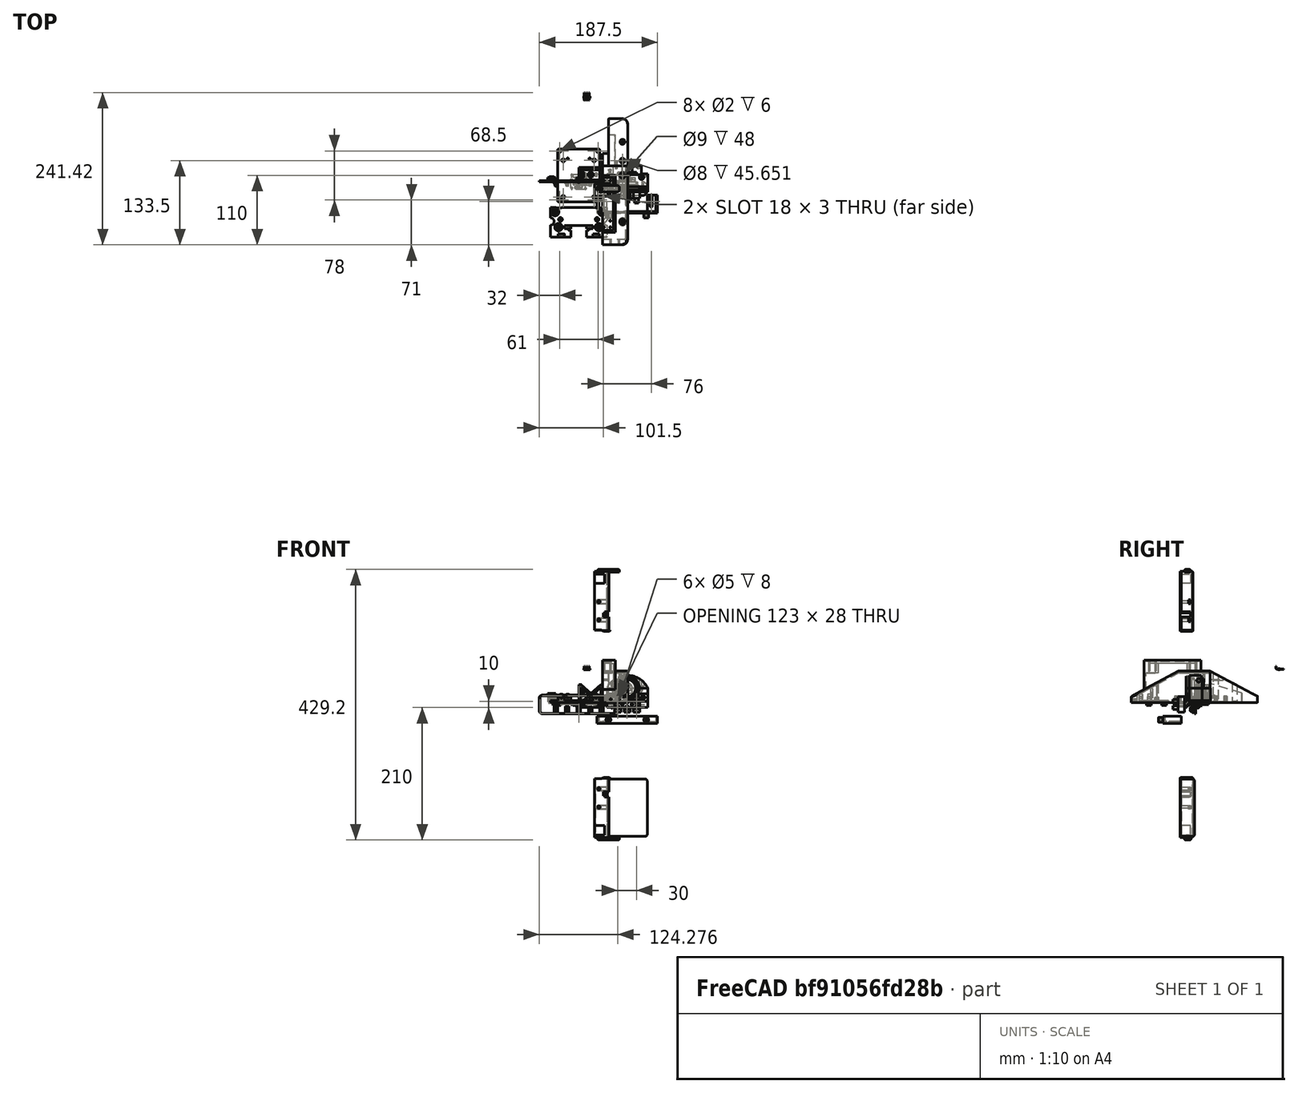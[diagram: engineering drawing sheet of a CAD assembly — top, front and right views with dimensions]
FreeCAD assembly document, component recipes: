
FREECAD ASSEMBLY — COMPONENT RECIPES ("BigOleYellow")

This assembly document has 16 components, labeled P0..P15 below (a component is one placed body or linked part). 9 of them carry a construction recipe — the FreeCAD feature program that regenerates the part from scratch, quoted from this document or its linked companion documents; the rest are supplied as boundary geometry only. No exploded tour is included for this assembly.
COMPONENT P0 — recipe-attached ("RearHullLeftBody", modeled in this document).
Construction recipe (the document's own serialized feature program — sketch geometry with constraints, then the solid features built on it; lengths are millimeters unless a unit is written):

FEATURE [Sketcher::SketchObject] Sketch015  label="RHLBBasePadSketch"
  FullyConstrained = true
  MapMode = 5
  Placement = pos=(0,0,0) rot=(0.57735,0.57735,0.57735;2.0944rad)
  Support = -> [YZ_Plane049]
  expr: Constraints[3] = Spreadsheet.rearhull_height
  expr: Constraints[4] = Spreadsheet.rearhull_length
  sketch-geometry (3):
    g0: LineSegment StartX=-2.83791e-11 StartY=40 StartZ=0 EndX=-2.83768e-11 EndY=0 EndZ=0
    g1: LineSegment StartX=-2.83768e-11 StartY=0 StartZ=0 EndX=75 EndY=-2e-16 EndZ=0
    g2: LineSegment StartX=75 StartY=-2e-16 StartZ=0 EndX=-2.83791e-11 EndY=40 EndZ=0
  constraints (7):
    c: Coincident(g0,g1)
    c: Coincident(g1,g2)
    c: Coincident(g2,g0)
    c: DistanceY(g0,g0) = 40
    c: DistanceX(g1,g1) = 75
    c: Tangent(g1,g-1)
    c: Tangent(g0,g-2)
FEATURE [PartDesign::Pad] Pad005  label="RHLBBasePad"
  Direction = (1,-2e-16,3e-16)
  Length = 30
  Length2 = 10
  Placement = pos=(0,0,0) rot=(1,1,1;2.0944rad)
  Profile = -> Sketch015
  ReferenceAxis = -> Sketch015 [N_Axis]
  Type = 0
  expr: Length = Spreadsheet.rearhull_width
FEATURE [PartDesign::Plane] DatumPlane009  label="RHLBBoltsPlane"
  AttachmentOffset = pos=(0,0,8) rot=(0,0,1;0rad)
  Length = 81.1245
  MapMode = 5
  Placement = pos=(0,0,-8) rot=(0,1,0;3.14159rad)
  ResizeMode = 0
  Support = -> [XY_Plane049]
  Width = 116.125
  expr: .AttachmentOffset.Base.z = <<chassis_spreadsheet>>.hull_base_height - <<chassis_spreadsheet>>.plate_thickness
FEATURE [Sketcher::SketchObject] Sketch016  label="RHLBBoltHolesSketch"
  ExternalGeometry = -> [Pad005]
  FullyConstrained = true
  MapMode = 5
  Placement = pos=(0,0,-8) rot=(0,1,0;3.14159rad)
  Support = -> [DatumPlane009]
  expr: Constraints[0] = -Spreadsheet.outer_hole_to_edge
  expr: Constraints[2] = Spreadsheet.outer_hole_dist_fb
  expr: Constraints[3] = Spreadsheet.outer_hole_from_rear
  expr: Constraints[4] = Spreadsheet.outer_hole_diameter
  sketch-geometry (2):
    g0: Circle CenterX=-8 CenterY=38.5 CenterZ=0 NormalX=0 NormalY=0 NormalZ=1 AngleXU=0 Radius=2
    g1: Circle CenterX=-8 CenterY=8.5 CenterZ=0 NormalX=0 NormalY=0 NormalZ=1 AngleXU=0 Radius=2
  constraints (6):
    c: DistanceX(g-4,g0) = -8
    c: Vertical(g1,g0)
    c: DistanceY(g1,g0) = 30
    c: DistanceY(g0,g-4) = 36.5
    c: Diameter(g0) = 4
    c: Equal(g0,g1)
FEATURE [Sketcher::SketchObject] Sketch017  label="RHLBBoltAccessSketch"
  ExternalGeometry = -> [Sketch016]
  FullyConstrained = true
  MapMode = 5
  Placement = pos=(0,0,-8) rot=(0,1,0;3.14159rad)
  Support = -> [DatumPlane009]
  expr: Constraints[1] = Spreadsheet.m4_bolt_access_diameter
  sketch-geometry (2):
    g0: Circle CenterX=-8 CenterY=8.5 CenterZ=0 NormalX=0 NormalY=0 NormalZ=1 AngleXU=0 Radius=4
    g1: Circle CenterX=-8 CenterY=38.5 CenterZ=0 NormalX=0 NormalY=0 NormalZ=1 AngleXU=0 Radius=4
  constraints (4):
    c: Equal(g1,g0)
    c: Diameter(g1) = 8
    c: Coincident(g1,g-3)
    c: Coincident(g0,g-4)
FEATURE [Sketcher::SketchObject] Sketch018  label="RHLBCutoutSketch"
  FullyConstrained = true
  MapMode = 5
  Placement = pos=(30,-1.33e-14,1e-14) rot=(0.57735,0.57735,0.57735;2.0944rad)
  Support = -> [Pad005]
  expr: Constraints[5] = Spreadsheet.rearhull_cutout_lower_height
  expr: Constraints[6] = Spreadsheet.rearhull_cutout_height
  expr: Constraints[7] = Spreadsheet.rearhull_cutout_length
  sketch-geometry (4):
    g0: LineSegment StartX=-2.8372e-11 StartY=20 StartZ=0 EndX=-2.83755e-11 EndY=0 EndZ=0
    g1: LineSegment StartX=-2.83755e-11 StartY=0 StartZ=0 EndX=50 EndY=-3.86e-14 EndZ=0
    g2: LineSegment StartX=50 StartY=-3.86e-14 StartZ=0 EndX=50 EndY=5 EndZ=0
    g3: LineSegment StartX=50 StartY=5 StartZ=0 EndX=-2.8372e-11 EndY=20 EndZ=0
  constraints (10):
    c: Coincident(g0,g1)
    c: Coincident(g1,g2)
    c: Coincident(g2,g3)
    c: Coincident(g3,g0)
    c: Vertical(g2)
    c: DistanceY(g2,g2) = 5
    c: DistanceY(g0,g0) = 20
    c: DistanceX(g1,g1) = 50
    c: Tangent(g1,g-1)
    c: Tangent(g0,g-2)
FEATURE [PartDesign::Pocket] Pocket007  label="RHLBCutout"
  BaseFeature = -> Pad005
  Direction = (-1,7e-16,-3e-16)
  Length = 10
  Length2 = 5
  Placement = pos=(0,0,0) rot=(1,1,1;2.0944rad)
  Profile = -> Sketch018
  ReferenceAxis = -> Sketch018 [N_Axis]
  Type = 0
  expr: Length = Spreadsheet.rearhull_cutout_width
FEATURE [Sketcher::SketchObject] Sketch019  label="RHLBTabSketch"
  ExternalGeometry = -> [Pocket007]
  FullyConstrained = true
  MapMode = 5
  Placement = pos=(30,-2e-14,1.33e-14) rot=(0.57735,0.57735,0.57735;2.0944rad)
  Support = -> [Pocket007]
  expr: Constraints[10] = Spreadsheet.mid_hull_tab_height
  expr: Constraints[8] = Spreadsheet.mid_hull_tab_length
  expr: Constraints[9] = Spreadsheet.plate_thickness
  sketch-geometry (4):
    g0: LineSegment StartX=-2.84158e-11 StartY=27 StartZ=0 EndX=20 EndY=27 EndZ=0
    g1: LineSegment StartX=20 StartY=27 StartZ=0 EndX=20 EndY=25 EndZ=0
    g2: LineSegment StartX=20 StartY=25 StartZ=0 EndX=-2.84288e-11 EndY=25 EndZ=0
    g3: LineSegment StartX=-2.84288e-11 StartY=25 StartZ=0 EndX=-2.84158e-11 EndY=27 EndZ=0
  constraints (11):
    c: Coincident(g0,g1)
    c: Coincident(g1,g2)
    c: Coincident(g2,g3)
    c: Coincident(g3,g0)
    c: Vertical(g1)
    c: Horizontal(g0)
    c: Horizontal(g2)
    c: Tangent(g3,g-3)
    c: DistanceX(g2,g2) = 20
    c: DistanceY(g1,g1) = 2
    c: DistanceY(g-4,g2) = 25
FEATURE [PartDesign::Pad] Pad006  label="RHLBTab"
  BaseFeature = -> Pocket007
  Direction = (1,-9e-16,6e-16)
  Length = 10
  Length2 = 10
  Placement = pos=(0,0,0) rot=(1,1,1;2.0944rad)
  Profile = -> Sketch019
  ReferenceAxis = -> Sketch019 [N_Axis]
  Refine = true
  Type = 0
  expr: Length = Spreadsheet.mid_hull_tab_width
FEATURE [PartDesign::Pad] Pad018  label="RHLBHullBase"
  BaseFeature = -> Pad006
  Direction = (6e-16,-1.2e-15,-1)
  Length = 10
  Length2 = 10
  Placement = pos=(0,0,0) rot=(1,1,1;2.0944rad)
  Profile = -> Pad006 [Face2]
  Refine = true
  Type = 0
  expr: Length = <<chassis_spreadsheet>>.hull_base_height
FEATURE [PartDesign::Pocket] Pocket005  label="RHLBBoltHoles"
  BaseFeature = -> Pad018
  Direction = (0,0,1)
  Length = 5
  Length2 = 5
  Placement = pos=(0,0,0) rot=(1,1,1;2.0944rad)
  Profile = -> Sketch016
  ReferenceAxis = -> Sketch016 [N_Axis]
  Reversed = true
  Type = 1
FEATURE [PartDesign::Pocket] Pocket006  label="RHLBBoltAccess"
  BaseFeature = -> Pocket005
  Direction = (0,0,1)
  Length = 5
  Length2 = 5
  Placement = pos=(0,0,0) rot=(1,1,1;2.0944rad)
  Profile = -> Sketch017
  ReferenceAxis = -> Sketch017 [N_Axis]
  Type = 1
FEATURE [PartDesign::Fillet] Fillet002
  Base = -> Pocket006 [Edge7]
  BaseFeature = -> Pocket006
  Placement = pos=(0,0,0) rot=(1,1,1;2.0944rad)
  Radius = 8
  SupportTransform = false
  UseAllEdges = false
FEATURE [PartDesign::Fillet] Fillet003
  Base = -> Fillet002 [Edge9,Edge22,Edge21,Edge23,Edge5,Edge10,Edge1,Edge4,Edge14]
  BaseFeature = -> Fillet002
  Placement = pos=(0,0,0) rot=(1,1,1;2.0944rad)
  Radius = 0.4
  SupportTransform = false
  UseAllEdges = false
FEATURE [PartDesign::Body] Body006  label="RearHullLeftBody"
  Group = -> [Sketch015,Pad005,Pocket007,Pad006,Pad018,DatumPlane009,Sketch016,Pocket005,Sketch017,Pocket006,Sketch018,Sketch019,Fillet002,Fillet003]
  Origin = -> Origin049
  Placement = pos=(-77.5,25,13) rot=(1,0,0;0rad)
  Tip = -> Fillet003
COMPONENT P1 — recipe-attached ("Hull2_Body", modeled in this document).
Construction recipe (the document's own serialized feature program — sketch geometry with constraints, then the solid features built on it; lengths are millimeters unless a unit is written):

FEATURE [Sketcher::SketchObject] Sketch050  label="Hull2ProfileSketch"
  FullyConstrained = true
  MapMode = 5
  Placement = pos=(0,0,0) rot=(0.57735,0.57735,0.57735;2.0944rad)
  Support = -> [YZ_Plane059]
  expr: Constraints[11] = <<chassis_spreadsheet>>.hull2_front_step_height
  expr: Constraints[12] = <<chassis_spreadsheet>>.hull2_slope_length
  expr: Constraints[7] = <<chassis_spreadsheet>>.hull2_length
  expr: Constraints[8] = <<chassis_spreadsheet>>.hull2_top
  sketch-geometry (5):
    g0: LineSegment StartX=-62.5 StartY=10 StartZ=0 EndX=-62.5 EndY=1.8e-15 EndZ=0
    g1: LineSegment StartX=12.5 StartY=50 StartZ=0 EndX=-62.5 EndY=10 EndZ=0
    g2: LineSegment StartX=-62.5 StartY=1.8e-15 StartZ=0 EndX=62.5 EndY=0 EndZ=0
    g3: LineSegment StartX=62.5 StartY=0 StartZ=0 EndX=62.5 EndY=50 EndZ=0
    g4: LineSegment StartX=62.5 StartY=50 StartZ=0 EndX=12.5 EndY=50 EndZ=0
  constraints (14):
    c: Vertical(g0)
    c: Coincident(g1,g0)
    c: Coincident(g2,g3)
    c: Vertical(g3)
    c: Coincident(g3,g4)
    c: Horizontal(g4)
    c: Coincident(g0,g2)
    c: DistanceX(g2,g2) = 125
    c: DistanceY(g3,g3) = 50
    c: Coincident(g1,g4)
    c: Symmetric(g0,g2,g-2)
    c: DistanceY(g0,g0) = 10
    c: DistanceX(g0,g1) = 75
    c: PointOnObject(g2,g-1)
FEATURE [PartDesign::Pad] Pad026  label="Hull2Profile"
  Direction = (1,-2e-16,3e-16)
  Length = 40
  Length2 = 10
  Placement = pos=(0,0,0) rot=(1,1,1;2.0944rad)
  Profile = -> Sketch050
  ReferenceAxis = -> Sketch050 [N_Axis]
  Type = 0
  expr: Length = <<chassis_spreadsheet>>.hull2_front_width
FEATURE [PartDesign::Plane] DatumPlane013
  AttachmentOffset = pos=(0,0,65) rot=(0,0,1;0rad)
  Length = 83.0278
  MapMode = 5
  Placement = pos=(0,0,65) rot=(0,0,1;0rad)
  ResizeMode = 0
  Support = -> [XY_Plane059]
  Width = 143.028
  expr: .AttachmentOffset.Base.z = <<chassis_spreadsheet>>.hull2_mount_height
FEATURE [Sketcher::SketchObject] Sketch051  label="Hull2MountingBossSketch"
  ExternalGeometry = -> [Pad026]
  FullyConstrained = true
  MapMode = 5
  Placement = pos=(0,0,65) rot=(0,0,1;0rad)
  Support = -> [DatumPlane013]
  expr: Constraints[10] = <<chassis_spreadsheet>>.hull2_mount_front
  expr: Constraints[11] = <<chassis_spreadsheet>>.attachment_plate_length + <<chassis_spreadsheet>>.attachment_plate_border * 2
  expr: Constraints[8] = <<chassis_spreadsheet>>.hull2_mount_x_offset
  sketch-geometry (4):
    g0: LineSegment StartX=19.5 StartY=47.5 StartZ=0 EndX=40 EndY=47.5 EndZ=0
    g1: LineSegment StartX=40 StartY=47.5 StartZ=0 EndX=40 EndY=-42.5 EndZ=0
    g2: LineSegment StartX=40 StartY=-42.5 StartZ=0 EndX=19.5 EndY=-42.5 EndZ=0
    g3: LineSegment StartX=19.5 StartY=-42.5 StartZ=0 EndX=19.5 EndY=47.5 EndZ=0
  constraints (12):
    c: Coincident(g0,g1)
    c: Coincident(g1,g2)
    c: Coincident(g2,g3)
    c: Coincident(g3,g0)
    c: Horizontal(g0)
    c: Horizontal(g2)
    c: Vertical(g1)
    c: Vertical(g3)
    c: DistanceX(g-1,g0) = 19.5
    c: PointOnObject(g0,g-3)
    c: DistanceY(g-4,g1) = 20
    c: DistanceY(g1,g1) = 90
FEATURE [PartDesign::Pad] Pad027  label="Hull2MountingBoss"
  BaseFeature = -> Pad026
  Direction = (0,0,1)
  Length = 10
  Length2 = 10
  Placement = pos=(0,0,0) rot=(1,1,1;2.0944rad)
  Profile = -> Sketch051
  ReferenceAxis = -> Sketch051 [N_Axis]
  Refine = true
  Type = 3
  UpToFace = -> Pad026 [Face2]
FEATURE [Sketcher::SketchObject] Sketch052  label="Hull2ChassisBoltsSketch"
  AttachmentOffset = pos=(0,0,2) rot=(0,0,1;0rad)
  ExternalGeometry = -> [Pad027]
  FullyConstrained = true
  MapMode = 5
  Placement = pos=(0,0,2) rot=(0,0,1;0rad)
  Support = -> [XY_Plane059]
  expr: .AttachmentOffset.Base.z = <<chassis_spreadsheet>>.plate_thickness
  expr: Constraints[1] = 2.5 mm
  expr: Constraints[2] = <<chassis_spreadsheet>>.hull2_mid_hole_from_frnt
  expr: Constraints[3] = <<chassis_spreadsheet>>.hull2_mid_hole_from_edge
  expr: Constraints[4] = <<chassis_spreadsheet>>.outer_hole_from_front
  expr: Constraints[5] = <<chassis_spreadsheet>>.outer_hole_to_edge
  sketch-geometry (2):
    g0: Circle CenterX=8 CenterY=47.5 CenterZ=0 NormalX=0 NormalY=0 NormalZ=1 AngleXU=0 Radius=1.25
    g1: Circle CenterX=8 CenterY=-26 CenterZ=0 NormalX=0 NormalY=0 NormalZ=1 AngleXU=0 Radius=1.25
  constraints (6):
    c: Equal(g1,g0)
    c: Diameter(g0) = 2.5
    c: DistanceY(g-3,g0) = 110
    c: DistanceX(g-3,g0) = 8
    c: DistanceY(g-3,g1) = 36.5
    c: DistanceX(g-3,g1) = 8
FEATURE [Sketcher::SketchObject] Sketch053  label="HUll2ApBorderSketch"
  ExternalGeometry = -> [Pad027]
  FullyConstrained = true
  MapMode = 5
  Placement = pos=(-2.16e-14,7.2e-15,65) rot=(0,0,-1;1.5708rad)
  Support = -> [Pad027]
  expr: Constraints[12] = <<chassis_spreadsheet>>.attachment_plate_border
  expr: Constraints[15] = <<chassis_spreadsheet>>.attachment_plate_border
  sketch-geometry (8):
    g0: LineSegment StartX=42.5 StartY=40 StartZ=0 EndX=39.5 EndY=40 EndZ=0
    g1: LineSegment StartX=39.5 StartY=40 StartZ=0 EndX=39.5 EndY=22.5 EndZ=0
    g2: LineSegment StartX=39.5 StartY=22.5 StartZ=0 EndX=-44.5 EndY=22.5 EndZ=0
    g3: LineSegment StartX=-44.5 StartY=22.5 StartZ=0 EndX=-44.5 EndY=40 EndZ=0
    g4: LineSegment StartX=-44.5 StartY=40 StartZ=0 EndX=-47.5 EndY=40 EndZ=0
    g5: LineSegment StartX=-47.5 StartY=40 StartZ=0 EndX=-47.5 EndY=19.5 EndZ=0
    g6: LineSegment StartX=-47.5 StartY=19.5 StartZ=0 EndX=42.5 EndY=19.5 EndZ=0
    g7: LineSegment StartX=42.5 StartY=19.5 StartZ=0 EndX=42.5 EndY=40 EndZ=0
  constraints (21):
    c: Horizontal(g0)
    c: Coincident(g0,g1)
    c: Coincident(g1,g2)
    c: Horizontal(g2)
    c: Coincident(g2,g3)
    c: Vertical(g3)
    c: Coincident(g3,g4)
    c: Coincident(g4,g5)
    c: Coincident(g5,g6)
    c: Coincident(g6,g7)
    c: Coincident(g0,g7)
    c: Vertical(g1)
    c: DistanceX(g0,g0) = 3
    c: Equal(g0,g4)
    c: Horizontal(g4)
    c: DistanceY(g6,g1) = 3
    c: Coincident(g4,g-3)
    c: Coincident(g5,g-4)
    c: Coincident(g0,g-5)
    c: Horizontal(g6)
    c: Vertical(g7)
FEATURE [PartDesign::Thickness] Thickness
  Base = -> Pad027 [Face11,Face8,Face3]
  BaseFeature = -> Pad027
  Intersection = false
  Join = 1
  Mode = 0
  Reversed = true
  SupportTransform = false
  Value = 3
FEATURE [PartDesign::Pad] Pad028  label="HUll2ApBorder"
  BaseFeature = -> Thickness
  Direction = (-3e-16,1e-16,1)
  Length = 2
  Length2 = 10
  Profile = -> Sketch053
  ReferenceAxis = -> Sketch053 [N_Axis]
  Type = 0
  expr: Length = <<chassis_spreadsheet>>.plate_thickness
FEATURE [Sketcher::SketchObject] Sketch054  label="HUll2ApHolesSketch"
  ExternalGeometry = -> [Sketch053]
  FullyConstrained = true
  MapMode = 5
  Placement = pos=(-2.16e-14,7.2e-15,65) rot=(0,0,1;0rad)
  Support = -> [Pad028]
  sketch-geometry (6):
    g0: Circle CenterX=27.5 CenterY=-24.5 CenterZ=0 NormalX=0 NormalY=0 NormalZ=1 AngleXU=0 Radius=1.25
    g1: Circle CenterX=27.5 CenterY=-34.5 CenterZ=0 NormalX=0 NormalY=0 NormalZ=1 AngleXU=0 Radius=1.25
    g2: Circle CenterX=37.5 CenterY=-34.5 CenterZ=0 NormalX=0 NormalY=0 NormalZ=1 AngleXU=0 Radius=1.25
    g3: Circle CenterX=27.5 CenterY=39.5 CenterZ=0 NormalX=0 NormalY=0 NormalZ=1 AngleXU=0 Radius=1.25
    g4: Circle CenterX=37.5 CenterY=39.5 CenterZ=0 NormalX=0 NormalY=0 NormalZ=1 AngleXU=0 Radius=1.25
    g5: Circle CenterX=27.5 CenterY=29.5 CenterZ=0 NormalX=0 NormalY=0 NormalZ=1 AngleXU=0 Radius=1.25
  constraints (18):
    c: Equal(g5,g4)
    c: Equal(g4,g3)
    c: Equal(g5,g2)
    c: Equal(g2,g1)
    c: Equal(g1,g0)
    c: DistanceX(g1,g2) = 10
    c: DistanceY(g1,g0) = 10
    c: DistanceX(g5,g4) = 10
    c: Diameter(g0) = 2.5
    c: Horizontal(g4,g3)
    c: DistanceY(g5,g3) = 10
    c: Vertical(g5,g3)
    c: Vertical(g0,g1)
    c: Horizontal(g2,g1)
    c: DistanceX(g-3,g3) = 5
    c: DistanceY(g3,g-3) = 5
    c: DistanceY(g-3,g1) = 5
    c: DistanceX(g-3,g1) = 5
FEATURE [Sketcher::SketchObject] Sketch056  label="Hull2SensorHolesSketch"
  ExternalGeometry = -> [Pad028]
  FullyConstrained = true
  MapMode = 5
  Placement = pos=(-2.78e-14,-62.5,4.16e-14) rot=(1,0,0;1.5708rad)
  Support = -> [Pad028]
  expr: Constraints[6] = <<chassis_spreadsheet>>.pim_tofl_hole_dist
  sketch-geometry (4):
    g0: Circle CenterX=26.8 CenterY=5 CenterZ=0 NormalX=0 NormalY=0 NormalZ=1 AngleXU=0 Radius=1.25
    g1: Circle CenterX=13.2 CenterY=5 CenterZ=0 NormalX=0 NormalY=0 NormalZ=1 AngleXU=0 Radius=1.25
    g2: LineSegment StartX=20 StartY=10 StartZ=0 EndX=20 EndY=2.49e-14 EndZ=0
    g3: LineSegment StartX=26.8 StartY=5 StartZ=0 EndX=13.2 EndY=5 EndZ=0
  constraints (10):
    c: Symmetric(g0,g1,g2)
    c: Equal(g1,g0)
    c: Diameter(g0) = 2.5
    c: Coincident(g3,g1)
    c: Symmetric(g2,g2,g3)
    c: Symmetric(g-3,g-3,g2)
    c: DistanceX(g1,g0) = 13.6
    c: PointOnObject(g2,g-3)
    c: PointOnObject(g2,g-4)
    c: Coincident(g3,g0)
FEATURE [Sketcher::SketchObject] Sketch057
  ExternalGeometry = -> [Sketch052]
  FullyConstrained = true
  MapMode = 5
  Support = -> [XY_Plane059]
  sketch-geometry (1):
    g0: Circle CenterX=8 CenterY=-26 CenterZ=0 NormalX=0 NormalY=0 NormalZ=1 AngleXU=0 Radius=6
  constraints (2):
    c: Coincident(g0,g-4)
    c: Diameter(g0) = 12
FEATURE [PartDesign::Pad] Pad029  label="Hull2FrontBoltBoss"
  BaseFeature = -> Pad028
  Direction = (0,0,1)
  Length = 10
  Length2 = 10
  Profile = -> Sketch057
  ReferenceAxis = -> Sketch057 [N_Axis]
  Type = 3
  UpToFace = -> Pad028 [Face2]
FEATURE [Sketcher::SketchObject] Sketch058
  ExternalGeometry = -> [Sketch052]
  FullyConstrained = true
  MapMode = 5
  Support = -> [XY_Plane059]
  sketch-geometry (1):
    g0: Circle CenterX=8 CenterY=47.5 CenterZ=0 NormalX=0 NormalY=0 NormalZ=1 AngleXU=0 Radius=6
  constraints (2):
    c: Coincident(g0,g-4)
    c: Diameter(g0) = 12
FEATURE [PartDesign::Pad] Pad030  label="Hull2RearBoltBoss"
  BaseFeature = -> Pad029
  Direction = (0,0,1)
  Length = 10
  Length2 = 10
  Profile = -> Sketch058
  ReferenceAxis = -> Sketch058 [N_Axis]
  Type = 3
  UpToFace = -> Pad029 [Face8]
FEATURE [Sketcher::SketchObject] Sketch059  label="Hull2APSupportSketchFront"
  ExternalGeometry = -> [Sketch053,Sketch054]
  FullyConstrained = true
  MapMode = 5
  Placement = pos=(-2.07e-14,6.9e-15,62) rot=(1,0,0;3.14159rad)
  Support = -> [Pad028]
  sketch-geometry (9):
    g0: LineSegment StartX=22.5 StartY=20.5 StartZ=0 EndX=28.8981 EndY=20.5 EndZ=0
    g1: LineSegment StartX=31.547 StartY=21.7123 StartZ=0 EndX=39.1489 EndY=30.5145 EndZ=0
    g2: LineSegment StartX=40 StartY=32.8022 StartZ=0 EndX=40 EndY=39.5 EndZ=0
    g3: LineSegment StartX=40 StartY=39.5 StartZ=0 EndX=22.5 EndY=39.5 EndZ=0
    g4: LineSegment StartX=22.5 StartY=39.5 StartZ=0 EndX=22.5 EndY=20.5 EndZ=0
    g5: ArcOfCircle CenterX=28.8981 CenterY=24 CenterZ=0 NormalX=0 NormalY=0 NormalZ=1 AngleXU=0 Radius=3.5 StartAngle=4.71239 EndAngle=5.57083
    g6: GeomPoint X=30.5 Y=20.5 Z=0
    g7: ArcOfCircle CenterX=36.5 CenterY=32.8022 CenterZ=0 NormalX=0 NormalY=0 NormalZ=1 AngleXU=0 Radius=3.5 StartAngle=5.57083 EndAngle=6.28319
    g8: GeomPoint X=40 Y=31.5 Z=0
  constraints (21):
    c: PointOnObject(g0,g-3)
    c: Horizontal(g0)
    c: Coincident(g2,g-4)
    c: Vertical(g2)
    c: Coincident(g2,g3)
    c: Coincident(g3,g-4)
    c: Coincident(g3,g4)
    c: Coincident(g4,g0)
    c: DistanceY(g0,g-6) = 4
    c: DistanceY(g8,g-7) = 3
    c: DistanceX(g-6,g6) = 3
    c: PointOnObject(g6,g0)
    c: PointOnObject(g6,g1)
    c: Tangent(g0,g5) = -1.5708
    c: Tangent(g1,g5) = -1.5708
    c: PointOnObject(g8,g1)
    c: PointOnObject(g8,g2)
    c: Tangent(g1,g7) = -1.5708
    c: Tangent(g2,g7) = -1.5708
    c: Equal(g7,g5)
    c: Diameter(g7) = 7
FEATURE [PartDesign::Pad] Pad031  label="Hull2APSupportFront"
  BaseFeature = -> Pad030
  Direction = (3e-16,-1e-16,-1)
  Length = 15
  Length2 = 10
  Profile = -> Sketch059
  ReferenceAxis = -> Sketch059 [N_Axis]
  Type = 0
FEATURE [Sketcher::SketchObject] Sketch060  label="Hull2APSupportSketchRear"
  ExternalGeometry = -> [Sketch059,Sketch053]
  FullyConstrained = true
  MapMode = 5
  Placement = pos=(-2.07e-14,6.9e-15,62) rot=(1,0,0;3.14159rad)
  Support = -> [Pad028]
  sketch-geometry (9):
    g0: LineSegment StartX=40 StartY=-44.5 StartZ=0 EndX=40 EndY=-37.8022 EndZ=0
    g1: LineSegment StartX=39.1489 StartY=-35.5145 StartZ=0 EndX=31.547 EndY=-26.7123 EndZ=0
    g2: LineSegment StartX=28.8981 StartY=-25.5 StartZ=0 EndX=22.5 EndY=-25.5 EndZ=0
    g3: LineSegment StartX=22.5 StartY=-25.5 StartZ=0 EndX=22.5 EndY=-44.5 EndZ=0
    g4: ArcOfCircle CenterX=28.8981 CenterY=-29 CenterZ=0 NormalX=0 NormalY=0 NormalZ=1 AngleXU=0 Radius=3.5 StartAngle=0.712358 EndAngle=1.5708
    g5: GeomPoint X=30.5 Y=-25.5 Z=0
    g6: ArcOfCircle CenterX=36.5 CenterY=-37.8022 CenterZ=0 NormalX=0 NormalY=0 NormalZ=1 AngleXU=0 Radius=3.5 StartAngle=0 EndAngle=0.712358
    g7: GeomPoint X=40 Y=-36.5 Z=0
    g8: LineSegment StartX=22.5 StartY=-44.5 StartZ=0 EndX=40 EndY=-44.5 EndZ=0
  constraints (21):
    c: Coincident(g-10,g0)
    c: Vertical(g0)
    c: Horizontal(g2)
    c: Coincident(g2,g3)
    c: Coincident(g3,g-10)
    c: Vertical(g3)
    c: Equal(g3,g-9)
    c: PointOnObject(g5,g2)
    c: PointOnObject(g5,g1)
    c: Tangent(g2,g4) = -1.5708
    c: Tangent(g1,g4) = -1.5708
    c: PointOnObject(g7,g0)
    c: PointOnObject(g7,g1)
    c: Tangent(g0,g6) = -1.5708
    c: Tangent(g1,g6) = -1.5708
    c: Equal(g2,g-3)
    c: Equal(g0,g-7)
    c: Equal(g4,g6)
    c: Equal(g6,g-6)
    c: Coincident(g8,g3)
    c: Coincident(g8,g0)
FEATURE [PartDesign::Pad] Pad032  label="Hull2APSupportRear"
  BaseFeature = -> Pad031
  Direction = (3e-16,-1e-16,-1)
  Length = 15
  Length2 = 10
  Profile = -> Sketch060
  ReferenceAxis = -> Sketch060 [N_Axis]
  Type = 0
FEATURE [PartDesign::Hole] Hole003  label="HUll2ApHoles"
  BaseFeature = -> Pad032
  CustomThreadClearance = 0
  Depth = 15
  DepthType = 0
  Diameter = 2.05
  DrillForDepth = false
  DrillPoint = 1
  DrillPointAngle = 118
  HoleCutCountersinkAngle = 90
  HoleCutCustomValues = false
  HoleCutDepth = 0
  HoleCutDiameter = 6.1
  HoleCutType = 0
  ModelThread = false
  Profile = -> Sketch054
  Refine = true
  Tapered = false
  TaperedAngle = 90
  ThreadClass = 0
  ThreadDepth = 15
  ThreadDepthType = 0
  ThreadDirection = 0
  ThreadFit = 0
  ThreadSize = 8
  ThreadType = 1
  Threaded = true
  UseCustomThreadClearance = false
FEATURE [PartDesign::Hole] Hole005  label="Hull2ChassisBolts"
  BaseFeature = -> Hole003
  CustomThreadClearance = 0
  Depth = 25
  DepthType = 0
  Diameter = 2.9
  DrillForDepth = false
  DrillPoint = 1
  DrillPointAngle = 118
  HoleCutCountersinkAngle = 90
  HoleCutCustomValues = false
  HoleCutDepth = 0
  HoleCutDiameter = 6.1
  HoleCutType = 0
  ModelThread = false
  Profile = -> Sketch052
  Tapered = false
  TaperedAngle = 90
  ThreadClass = 0
  ThreadDepth = 25
  ThreadDepthType = 0
  ThreadDirection = 0
  ThreadFit = 0
  ThreadSize = 8
  ThreadType = 1
  Threaded = false
  UseCustomThreadClearance = false
FEATURE [PartDesign::Hole] Hole006  label="Hull2ChassisBoltAccess"
  BaseFeature = -> Hole005
  CustomThreadClearance = 0
  Depth = 297.661
  DepthType = 1
  Diameter = 9
  DrillForDepth = false
  DrillPoint = 1
  DrillPointAngle = 118
  HoleCutCountersinkAngle = 90
  HoleCutCustomValues = false
  HoleCutDepth = 0
  HoleCutDiameter = 6.1
  HoleCutType = 0
  ModelThread = false
  Profile = -> Sketch052
  Reversed = true
  Tapered = false
  TaperedAngle = 90
  ThreadClass = 0
  ThreadDepth = 297.661
  ThreadDepthType = 0
  ThreadDirection = 0
  ThreadFit = 0
  ThreadSize = 16
  ThreadType = 1
  Threaded = false
  UseCustomThreadClearance = false
FEATURE [Sketcher::SketchObject] Sketch061
  ExternalGeometry = -> [Pad028]
  FullyConstrained = true
  MapMode = 5
  Support = -> [XY_Plane059]
  sketch-geometry (4):
    g0: LineSegment StartX=3 StartY=-59.5 StartZ=0 EndX=40 EndY=-59.5 EndZ=0
    g1: LineSegment StartX=40 StartY=-59.5 StartZ=0 EndX=40 EndY=-53.5 EndZ=0
    g2: LineSegment StartX=40 StartY=-53.5 StartZ=0 EndX=3 EndY=-53.5 EndZ=0
    g3: LineSegment StartX=3 StartY=-53.5 StartZ=0 EndX=3 EndY=-59.5 EndZ=0
  constraints (10):
    c: Coincident(g0,g1)
    c: Coincident(g1,g2)
    c: Coincident(g2,g3)
    c: Coincident(g3,g0)
    c: Horizontal(g2)
    c: Vertical(g1)
    c: Vertical(g3)
    c: Coincident(g0,g-3)
    c: Coincident(g0,g-3)
    c: DistanceY(g1,g1) = 6
FEATURE [PartDesign::Pad] Pad033
  BaseFeature = -> Hole006
  Direction = (0,0,1)
  Length = 10
  Length2 = 10
  Profile = -> Sketch061
  ReferenceAxis = -> Sketch061 [N_Axis]
  Refine = true
  Type = 2
FEATURE [PartDesign::Hole] Hole004  label="Hull2SensorHoles"
  BaseFeature = -> Pad033
  CustomThreadClearance = 0
  Depth = 8
  DepthType = 0
  Diameter = 2.05
  DrillForDepth = false
  DrillPoint = 1
  DrillPointAngle = 118
  HoleCutCountersinkAngle = 90
  HoleCutCustomValues = false
  HoleCutDepth = 0
  HoleCutDiameter = 6.1
  HoleCutType = 0
  ModelThread = false
  Profile = -> Sketch056
  Tapered = false
  TaperedAngle = 90
  ThreadClass = 0
  ThreadDepth = 8
  ThreadDepthType = 0
  ThreadDirection = 0
  ThreadFit = 0
  ThreadSize = 8
  ThreadType = 1
  Threaded = true
  UseCustomThreadClearance = false
FEATURE [PartDesign::Fillet] Fillet009
  Base = -> Hole004 [Edge75]
  BaseFeature = -> Hole004
  Radius = 8
  SupportTransform = false
  UseAllEdges = false
FEATURE [PartDesign::Fillet] Fillet010
  Base = -> Fillet009 [Edge42,Edge16,Edge66,Edge43,Edge50,Edge61,Edge76,Edge60,Edge51]
  BaseFeature = -> Fillet009
  Radius = 2
  SupportTransform = false
  UseAllEdges = false
FEATURE [PartDesign::Body] Body012  label="Hull2_Body"
  Group = -> [Sketch050,Pad026,DatumPlane013,Sketch051,Pad027,Thickness,Pad028,Sketch052,Pad029,Pad030,Pad031,Pad032,Sketch053,Sketch054,Hole003,Sketch056,Sketch057,Sketch058,Hole005,Hole006,Sketch059,Sketch060,Sketch061,Pad033,Hole004,Fillet009,Fillet010]
  Origin = -> Origin059
  Placement = pos=(-77.5,-37.5,3) rot=(0,0,1;0rad)
  Tip = -> Fillet010
COMPONENT P2 — recipe-attached ("RaspberryPi3A+ v8", a linked part whose construction recipe lives in a companion FreeCAD document of the same project; that document's serialized recipe follows).
Construction recipe (the companion document, serialized — sketch geometry with constraints, then the solid features built on it; lengths are millimeters unless a unit is written):

FCSTD DOCUMENT  (FreeCAD 0.21R33771 (Git))
Label: RaspberryPi3a+
License: All rights reserved
LicenseURL: http://en.wikipedia.org/wiki/All_rights_reserved
objects: Part::Feature×36, App::Part×5, PartDesign::Line×4, Spreadsheet::Sheet×1
note: 40 computed .brp shape members not serialized (recipe doc carries the construction recipe); baked Part::Feature solids carry a one-line shape summary decoded from their .brp

FEATURE [Part::Feature] Part__Feature090  label="CSI HEader"
  shape: bbox 2.6 x 5.5 x 22 mm, 6 faces (baked)
FEATURE [Part::Feature] Part__Feature091  label="PiLogoCan v1"
  Placement = pos=(-32,-2.2e-15,30) rot=(0,0,1;0rad)
  shape: bbox 10.5 x 3 x 13.25 mm, 71 faces (baked)
FEATURE [Part::Feature] Part__Feature092  label="BCM Chip v1"
  Placement = pos=(-33.0271,-0.0600321,30.4516) rot=(0,0,1;0rad)
  shape: bbox 14 x 2.5 x 14 mm, 10 faces (baked)
FEATURE [App::Part] USBHost
  Group = -> [Part__Feature090,Part__Feature091,Part__Feature092]
  Origin = -> Origin018
FEATURE [Part::Feature] Part__Feature093  label="shield001"
  Placement = pos=(9e-16,1.8e-15,0) rot=(0,0,1;0rad)
  shape: bbox 5.846 x 7.775 x 3.404 mm, 350 faces (baked)
FEATURE [Part::Feature] Part__Feature094  label="socket_housing001"
  Placement = pos=(3e-15,2e-15,0) rot=(0,0,1;0rad)
  shape: bbox 4.232 x 6.852 x 2.152 mm, 338 faces (baked)
FEATURE [Part::Feature] Part__Feature095  label="socket_plate001"
  Placement = pos=(3e-15,2e-15,0) rot=(0,0,1;0rad)
  shape: bbox 3.38 x 6.8 x 0.31 mm, 84 faces (baked)
FEATURE [Part::Feature] Part__Feature096  label="terminal005"
  Placement = pos=(3e-15,2e-15,0) rot=(0,0,1;0rad)
  shape: bbox 3.22 x 0.35 x 1.72 mm, 36 faces (baked)
FEATURE [Part::Feature] Part__Feature097  label="terminal006"
  Placement = pos=(1.3,0,0) rot=(0,0,1;0rad)
  shape: bbox 3.22 x 0.35 x 1.72 mm, 36 faces (baked)
FEATURE [Part::Feature] Part__Feature098  label="terminal007"
  Placement = pos=(0.65,1.8e-14,1.3e-14) rot=(0,0,1;0rad)
  shape: bbox 3.22 x 0.35 x 1.72 mm, 36 faces (baked)
FEATURE [Part::Feature] Part__Feature099  label="terminal008"
  Placement = pos=(-0.65,1.78e-14,0) rot=(0,0,1;0rad)
  shape: bbox 3.22 x 0.35 x 1.72 mm, 36 faces (baked)
FEATURE [Part::Feature] Part__Feature100  label="terminal009"
  Placement = pos=(-1.3,1.78e-14,0) rot=(0,0,1;0rad)
  shape: bbox 3.22 x 0.35 x 1.72 mm, 36 faces (baked)
FEATURE [App::Part] USB_Micro_Socket_Housing_v002  label="USB Micro Socket Housing v002"
  Group = -> [Part__Feature093,Part__Feature094,Part__Feature095,Part__Feature096,Part__Feature097,Part__Feature098,Part__Feature099,Part__Feature100]
  Origin = -> Origin019
  Placement = pos=(-21.1892,1.50001,23.875) rot=(-0.57735,-0.57735,-0.57735;2.0944rad)
FEATURE [Part::Feature] Part__Feature101  label="GPIO"
  shape: bbox 50 x 2.3 x 5 mm, 6 faces (baked)
FEATURE [Part::Feature] Part__Feature102  label="COMPOUND004"
  shape: bbox 64 x 8.7 x 55 mm, 254 faces, 41 solids (baked)
FEATURE [App::Part] Board  label="Board001"
  Group = -> [USBHost,USB_Micro_Socket_Housing_v002,Part__Feature101,Part__Feature102]
  Origin = -> Origin020
FEATURE [Part::Feature] Part__Feature103  label="HDMI_socket_cover"
  Placement = pos=(-20,0,0) rot=(0,0,1;0rad)
  shape: bbox 16.2 x 8 x 9 mm, 311 faces (baked)
FEATURE [Part::Feature] Part__Feature104  label="HDMI_socket_inside"
  Placement = pos=(-20,-4e-15,0) rot=(0,0,1;0rad)
  shape: bbox 15 x 6.1 x 7.6 mm, 598 faces (baked)
FEATURE [Part::Feature] Part__Feature105  label="HDMI_socket_large_pin"
  Placement = pos=(-201.766,0.45,76.5103) rot=(0.57735,0.57735,-0.57735;2.0944rad)
  shape: bbox 0.65 x 3.842 x 7.55 mm, 54 faces (baked)
FEATURE [Part::Feature] Part__Feature106  label="HDMI_socket_small_pin"
  Placement = pos=(-202.266,-0.25,76.5103) rot=(0.57735,0.57735,-0.57735;2.0944rad)
  shape: bbox 0.65 x 3.08 x 7.55 mm, 54 faces (baked)
FEATURE [Part::Feature] Part__Feature107  label="HDMI_socket_large_pin001"
  Placement = pos=(-202.766,0.45,76.5103) rot=(0.57735,0.57735,-0.57735;2.0944rad)
  shape: bbox 0.65 x 3.842 x 7.55 mm, 54 faces (baked)
FEATURE [Part::Feature] Part__Feature108  label="HDMI_socket_large_pin002"
  Placement = pos=(-203.766,0.45,76.5103) rot=(0.57735,0.57735,-0.57735;2.0944rad)
  shape: bbox 0.65 x 3.842 x 7.55 mm, 54 faces (baked)
FEATURE [Part::Feature] Part__Feature109  label="HDMI_socket_large_pin003"
  Placement = pos=(-204.766,0.45,76.5103) rot=(0.57735,0.57735,-0.57735;2.0944rad)
  shape: bbox 0.65 x 3.842 x 7.55 mm, 54 faces (baked)
FEATURE [Part::Feature] Part__Feature110  label="HDMI_socket_large_pin004"
  Placement = pos=(-205.766,0.45,76.5103) rot=(0.57735,0.57735,-0.57735;2.0944rad)
  shape: bbox 0.65 x 3.842 x 7.55 mm, 54 faces (baked)
FEATURE [Part::Feature] Part__Feature111  label="HDMI_socket_large_pin005"
  Placement = pos=(-206.766,0.45,76.5103) rot=(0.57735,0.57735,-0.57735;2.0944rad)
  shape: bbox 0.65 x 3.842 x 7.55 mm, 54 faces (baked)
FEATURE [Part::Feature] Part__Feature112  label="HDMI_socket_large_pin006"
  Placement = pos=(-207.766,0.45,76.5103) rot=(0.57735,0.57735,-0.57735;2.0944rad)
  shape: bbox 0.65 x 3.842 x 7.55 mm, 54 faces (baked)
FEATURE [Part::Feature] Part__Feature113  label="HDMI_socket_large_pin007"
  Placement = pos=(-208.766,0.45,76.5103) rot=(0.57735,0.57735,-0.57735;2.0944rad)
  shape: bbox 0.65 x 3.842 x 7.55 mm, 54 faces (baked)
FEATURE [Part::Feature] Part__Feature114  label="HDMI_socket_large_pin008"
  Placement = pos=(-209.766,0.45,76.5103) rot=(0.57735,0.57735,-0.57735;2.0944rad)
  shape: bbox 0.65 x 3.842 x 7.55 mm, 54 faces (baked)
FEATURE [Part::Feature] Part__Feature115  label="HDMI_socket_large_pin009"
  Placement = pos=(-210.766,0.45,76.5103) rot=(0.57735,0.57735,-0.57735;2.0944rad)
  shape: bbox 0.65 x 3.842 x 7.55 mm, 54 faces (baked)
FEATURE [Part::Feature] Part__Feature116  label="HDMI_socket_small_pin001"
  Placement = pos=(-203.266,-0.25,76.5103) rot=(0.57735,0.57735,-0.57735;2.0944rad)
  shape: bbox 0.65 x 3.08 x 7.55 mm, 54 faces (baked)
FEATURE [Part::Feature] Part__Feature117  label="HDMI_socket_small_pin002"
  Placement = pos=(-204.266,-0.25,76.5103) rot=(0.57735,0.57735,-0.57735;2.0944rad)
  shape: bbox 0.65 x 3.08 x 7.55 mm, 54 faces (baked)
FEATURE [Part::Feature] Part__Feature118  label="HDMI_socket_small_pin003"
  Placement = pos=(-205.266,-0.25,76.5103) rot=(0.57735,0.57735,-0.57735;2.0944rad)
  shape: bbox 0.65 x 3.08 x 7.55 mm, 54 faces (baked)
FEATURE [Part::Feature] Part__Feature119  label="HDMI_socket_small_pin004"
  Placement = pos=(-206.266,-0.25,76.5103) rot=(0.57735,0.57735,-0.57735;2.0944rad)
  shape: bbox 0.65 x 3.08 x 7.55 mm, 54 faces (baked)
FEATURE [Part::Feature] Part__Feature120  label="HDMI_socket_small_pin005"
  Placement = pos=(-207.266,-0.25,76.5103) rot=(0.57735,0.57735,-0.57735;2.0944rad)
  shape: bbox 0.65 x 3.08 x 7.55 mm, 54 faces (baked)
FEATURE [Part::Feature] Part__Feature121  label="HDMI_socket_small_pin006"
  Placement = pos=(-208.266,-0.25,76.5103) rot=(0.57735,0.57735,-0.57735;2.0944rad)
  shape: bbox 0.65 x 3.08 x 7.55 mm, 54 faces (baked)
FEATURE [Part::Feature] Part__Feature122  label="HDMI_socket_small_pin007"
  Placement = pos=(-209.266,-0.25,76.5103) rot=(0.57735,0.57735,-0.57735;2.0944rad)
  shape: bbox 0.65 x 3.08 x 7.55 mm, 54 faces (baked)
FEATURE [Part::Feature] Part__Feature123  label="HDMI_socket_small_pin008"
  Placement = pos=(-210.266,-0.25,76.5103) rot=(0.57735,0.57735,-0.57735;2.0944rad)
  shape: bbox 0.65 x 3.08 x 7.55 mm, 54 faces (baked)
FEATURE [App::Part] HDMI_socket_v1  label="HDMI_socket v1"
  Group = -> [Part__Feature103,Part__Feature104,Part__Feature105,Part__Feature106,Part__Feature107,Part__Feature108,Part__Feature109,Part__Feature110,Part__Feature111,Part__Feature112,Part__Feature113,Part__Feature114,Part__Feature115,Part__Feature116,Part__Feature117,Part__Feature118,Part__Feature119,Part__Feature120,Part__Feature121,Part__Feature122,Part__Feature123]
  Origin = -> Origin021
  Placement = pos=(5.95,4.925,22.15) rot=(0,0,1;0rad)
FEATURE [Part::Feature] Part__Feature124  label="USB A Receptacle SMT v1"
  Placement = pos=(13.6383,14.3386,-9.70035) rot=(-0.57735,0.57735,0.57735;2.0944rad)
  shape: bbox 14.94 x 8.955 x 14.63 mm, 587 faces (baked)
FEATURE [Part::Feature] Part__Feature125  label="SOLID002"
  shape: bbox 64 x 1.5 x 55 mm, 14 faces (baked)
FEATURE [PartDesign::Line] HoleAxis_1
  AttacherType = Attacher::AttachEngineLine
  Length = 3.52267
  MapMode = 19
  Placement = pos=(29,0,24.5) rot=(0,-0.707107,0.707107;3.14159rad)
  ResizeMode = 1
  Support = -> [Part__Feature125]
FEATURE [PartDesign::Line] HoleAxis_2
  AttacherType = Attacher::AttachEngineLine
  Length = 3.52267
  MapMode = 19
  Placement = pos=(-29,0,24.5) rot=(0,-0.707107,0.707107;3.14159rad)
  ResizeMode = 1
  Support = -> [Part__Feature125]
FEATURE [PartDesign::Line] HoleAxis_3
  AttacherType = Attacher::AttachEngineLine
  Length = 3.52267
  MapMode = 19
  Placement = pos=(29,0,-24.5) rot=(0,-0.707107,0.707107;3.14159rad)
  ResizeMode = 1
  Support = -> [Part__Feature125]
FEATURE [PartDesign::Line] HoleAxis_4
  AttacherType = Attacher::AttachEngineLine
  Length = 3.52267
  MapMode = 19
  Placement = pos=(-29,0,-24.5) rot=(0,-0.707107,0.707107;3.14159rad)
  ResizeMode = 1
  Support = -> [Part__Feature125]
FEATURE [App::Part] RaspberryPi3A__v8  label="RaspberryPi3A+ v8"
  Group = -> [Board,HDMI_socket_v1,Part__Feature124,Part__Feature125,HoleAxis_1,HoleAxis_2,HoleAxis_3,HoleAxis_4]
  Origin = -> Origin022
  Placement = pos=(0,0,0) rot=(0,0,1;3.14159rad)
FEATURE [Spreadsheet::Sheet] Spreadsheet001  label="RaspberryPiSheet"
  cells = A1='Raspberry PI; A2='hole_diameter; B2(hole_diameter)==2.5 mm; D2='board_width; E2(board_width)==65 mm; A3='width_between_holes; B3(width_between_holes)==49 mm; D3='board_length; E3(board_length)==56 mm; A4='length_between_holes; B4(length_between_holes)==58 mm
COMPONENT P3 — recipe-attached ("ChassisPlate", modeled in this document).
Construction recipe (the document's own serialized feature program — sketch geometry with constraints, then the solid features built on it; lengths are millimeters unless a unit is written):

FEATURE [Sketcher::SketchObject] Sketch032  label="YukonPiMountBaseSketch"
  FullyConstrained = true
  MapMode = 5
  Support = -> [XY_Plane057]
  expr: Constraints[10] = <<YukonSheet>>.length / 2 + <<chassis_spreadsheet>>.yukon_pi_y_offset
  expr: Constraints[7] = <<YukonSheet>>.length
  expr: Constraints[8] = <<YukonSheet>>.width
  sketch-geometry (4):
    g0: LineSegment StartX=-33.5 StartY=52 StartZ=0 EndX=33.5 EndY=52 EndZ=0
    g1: LineSegment StartX=33.5 StartY=52 StartZ=0 EndX=33.5 EndY=-32 EndZ=0
    g2: LineSegment StartX=33.5 StartY=-32 StartZ=0 EndX=-33.5 EndY=-32 EndZ=0
    g3: LineSegment StartX=-33.5 StartY=-32 StartZ=0 EndX=-33.5 EndY=52 EndZ=0
  constraints (11):
    c: Coincident(g0,g1)
    c: Coincident(g1,g2)
    c: Coincident(g2,g3)
    c: Coincident(g3,g0)
    c: Horizontal(g2)
    c: Vertical(g1)
    c: Vertical(g3)
    c: DistanceY(g1,g1) = 84
    c: DistanceX(g0,g0) = 67
    c: Symmetric(g0,g0,g-2)
    c: DistanceY(g-1,g0) = 52
FEATURE [PartDesign::Pad] Pad014  label="YukonPiMountBase"
  Direction = (0,0,1)
  Length = 2
  Length2 = 10
  Profile = -> Sketch032
  ReferenceAxis = -> Sketch032 [N_Axis]
  Type = 0
  expr: Length = <<chassis_spreadsheet>>.plate_thickness
FEATURE [Sketcher::SketchObject] Sketch033  label="YukonPiMountOuterDiamondSketch"
  FullyConstrained = true
  MapMode = 5
  Placement = pos=(0,0,2) rot=(0,0,1;0rad)
  Support = -> [Pad014]
  expr: Constraints[2] = <<chassis_spreadsheet>>.diamond_small_diam
  expr: Constraints[3] = <<chassis_spreadsheet>>.diamond_outer_pair_dist
  sketch-geometry (2):
    g0: Circle CenterX=-17.5 CenterY=36.5 CenterZ=0 NormalX=0 NormalY=0 NormalZ=1 AngleXU=0 Radius=1.25
    g1: Circle CenterX=17.5 CenterY=36.5 CenterZ=0 NormalX=0 NormalY=0 NormalZ=1 AngleXU=0 Radius=1.25
  constraints (5):
    c: Equal(g1,g0)
    c: Symmetric(g0,g1,g-2)
    c: Diameter(g1) = 2.5
    c: DistanceX(g0,g1) = 35
    c: DistanceY(g-1,g0) = 36.5
FEATURE [PartDesign::Pocket] Pocket  label="YukonPiMountOuterDiamondHoles"
  BaseFeature = -> Pad014
  Direction = (0,0,-1)
  Length = 5
  Length2 = 5
  Profile = -> Sketch033
  ReferenceAxis = -> Sketch033 [N_Axis]
  Type = 1
FEATURE [Sketcher::SketchObject] Sketch034  label="YukonPiMountYukonBossSketch"
  FullyConstrained = true
  MapMode = 5
  Placement = pos=(0,0,2) rot=(0,0,1;0rad)
  Support = -> [Pocket]
  expr: Constraints[12] = <<chassis_spreadsheet>>.yukon_pi_y_offset
  expr: Constraints[5] = <<chassis_spreadsheet>>.m25_boss_diameter
  expr: Constraints[6] = <<YukonSheet>>.width_spacing
  expr: Constraints[7] = <<YukonSheet>>.length_spacing
  sketch-geometry (5):
    g0: Circle CenterX=-30.5 CenterY=49 CenterZ=0 NormalX=0 NormalY=0 NormalZ=1 AngleXU=0 Radius=2.5
    g1: Circle CenterX=-30.5 CenterY=-29 CenterZ=0 NormalX=0 NormalY=0 NormalZ=1 AngleXU=0 Radius=2.5
    g2: Circle CenterX=30.5 CenterY=49 CenterZ=0 NormalX=0 NormalY=0 NormalZ=1 AngleXU=0 Radius=2.5
    g3: Circle CenterX=30.5 CenterY=-29 CenterZ=0 NormalX=0 NormalY=0 NormalZ=1 AngleXU=0 Radius=2.5
    g4: LineSegment StartX=-30.5 StartY=10 StartZ=0 EndX=30.5 EndY=10 EndZ=0
  constraints (13):
    c: Symmetric(g2,g0,g-2)
    c: Symmetric(g1,g3,g-2)
    c: Equal(g1,g0)
    c: Equal(g0,g2)
    c: Equal(g2,g3)
    c: Diameter(g2) = 5
    c: DistanceX(g0,g2) = 61
    c: DistanceY(g3,g2) = 78
    c: Horizontal(g4)
    c: Vertical(g4,g2)
    c: Vertical(g4,g0)
    c: Symmetric(g2,g3,g4)
    c: DistanceY(g-1,g4) = 10
FEATURE [PartDesign::Pad] Pad015  label="YukonPiMountYukonBoss"
  BaseFeature = -> Pocket
  Direction = (0,0,1)
  Length = 8
  Length2 = 10
  Profile = -> Sketch034
  ReferenceAxis = -> Sketch034 [N_Axis]
  Type = 0
  expr: Length = <<chassis_spreadsheet>>.boss_height
FEATURE [Sketcher::SketchObject] Sketch035  label="YukonPiMountPiBossSketch"
  FullyConstrained = true
  MapMode = 5
  Placement = pos=(0,0,2) rot=(0,0,1;0rad)
  Support = -> [Pad015]
  expr: Constraints[5] = <<chassis_spreadsheet>>.m25_boss_diameter
  expr: Constraints[6] = <<RaspberryPiSheet>>.width_between_holes
  expr: Constraints[8] = <<RaspberryPiSheet>>.length_between_holes
  sketch-geometry (4):
    g0: Circle CenterX=-24.5 CenterY=34 CenterZ=0 NormalX=0 NormalY=0 NormalZ=1 AngleXU=0 Radius=2.5
    g1: Circle CenterX=24.5 CenterY=34 CenterZ=0 NormalX=0 NormalY=0 NormalZ=1 AngleXU=0 Radius=2.5
    g2: Circle CenterX=-24.5 CenterY=-24 CenterZ=0 NormalX=0 NormalY=0 NormalZ=1 AngleXU=0 Radius=2.5
    g3: Circle CenterX=24.5 CenterY=-24 CenterZ=0 NormalX=0 NormalY=0 NormalZ=1 AngleXU=0 Radius=2.5
  constraints (10):
    c: Symmetric(g0,g1,g-2)
    c: Symmetric(g2,g3,g-2)
    c: Equal(g0,g1)
    c: Equal(g1,g3)
    c: Equal(g3,g2)
    c: Diameter(g0) = 5
    c: DistanceX(g0,g1) = 49
    c: Vertical(g1,g3)
    c: DistanceY(g3,g1) = 58
    c: DistanceY(g2,g-1) = 24
FEATURE [PartDesign::Pad] Pad016  label="YukonPiMountPiBoss"
  BaseFeature = -> Pad015
  Direction = (0,0,1)
  Length = 8
  Length2 = 10
  Profile = -> Sketch035
  ReferenceAxis = -> Sketch035 [N_Axis]
  Type = 0
  expr: Length = <<chassis_spreadsheet>>.boss_height
FEATURE [Sketcher::SketchObject] Sketch036  label="YukonPimountThreadSketch"
  ExternalGeometry = -> [Pad016]
  FullyConstrained = true
  MapMode = 5
  Placement = pos=(0,0,10) rot=(0,0,1;0rad)
  Support = -> [Pad016]
  expr: Constraints[15] = <<chassis_spreadsheet>>.m25_thread_diam
  sketch-geometry (8):
    g0: Circle CenterX=-30.5 CenterY=49 CenterZ=0 NormalX=0 NormalY=0 NormalZ=1 AngleXU=0 Radius=1
    g1: Circle CenterX=-24.5 CenterY=34 CenterZ=0 NormalX=0 NormalY=0 NormalZ=1 AngleXU=0 Radius=1
    g2: Circle CenterX=30.5 CenterY=49 CenterZ=0 NormalX=0 NormalY=0 NormalZ=1 AngleXU=0 Radius=1
    g3: Circle CenterX=24.5 CenterY=34 CenterZ=0 NormalX=0 NormalY=0 NormalZ=1 AngleXU=0 Radius=1
    g4: Circle CenterX=30.5 CenterY=-29 CenterZ=0 NormalX=0 NormalY=0 NormalZ=1 AngleXU=0 Radius=1
    g5: Circle CenterX=24.5 CenterY=-24 CenterZ=0 NormalX=0 NormalY=0 NormalZ=1 AngleXU=0 Radius=1
    g6: Circle CenterX=-24.5 CenterY=-24 CenterZ=0 NormalX=0 NormalY=0 NormalZ=1 AngleXU=0 Radius=1
    g7: Circle CenterX=-30.5 CenterY=-29 CenterZ=0 NormalX=0 NormalY=0 NormalZ=1 AngleXU=0 Radius=1
  constraints (16):
    c: Coincident(g0,g-3)
    c: Coincident(g1,g-4)
    c: Coincident(g2,g-5)
    c: Coincident(g3,g-6)
    c: Coincident(g5,g-8)
    c: Coincident(g6,g-9)
    c: Coincident(g7,g-10)
    c: Coincident(g4,g-7)
    c: Equal(g4,g5)
    c: Equal(g5,g7)
    c: Equal(g7,g6)
    c: Equal(g6,g1)
    c: Equal(g1,g3)
    c: Equal(g3,g2)
    c: Equal(g2,g0)
    c: Diameter(g0) = 2
FEATURE [PartDesign::Pocket] Pocket009  label="YukonPimountThread"
  BaseFeature = -> Pad016
  Direction = (0,0,-1)
  Length = 6
  Length2 = 5
  Profile = -> Sketch036
  ReferenceAxis = -> Sketch036 [N_Axis]
  Type = 0
  expr: Length = <<chassis_spreadsheet>>.m25_standoff_thread_length
FEATURE [PartDesign::Fillet] Fillet  label="YukonPimountCornerFillet"
  Base = -> Pocket009 [Edge5,Edge8,Edge1,Edge2]
  BaseFeature = -> Pocket009
  Radius = 2
  SupportTransform = false
  UseAllEdges = false
FEATURE [PartDesign::Body] Body011  label="YukonPiMount"
  Group = -> [Sketch032,Pad014,Sketch033,Pocket,Sketch034,Pad015,Sketch035,Pad016,Sketch036,Pocket009,Fillet]
  Origin = -> Origin057
  Placement = pos=(0,0,3) rot=(0,0,1;0rad)
  Tip = -> Fillet
COMPONENT P4 — recipe-attached ("Yukon", a linked part whose construction recipe lives in a companion FreeCAD document of the same project; that document's serialized recipe follows).
Construction recipe (the companion document, serialized — sketch geometry with constraints, then the solid features built on it; lengths are millimeters unless a unit is written):

FCSTD DOCUMENT  (FreeCAD 0.21R33771 (Git))
Label: YukonBoard
License: All rights reserved
LicenseURL: http://en.wikipedia.org/wiki/All_rights_reserved
objects: Sketcher::SketchObject×4, PartDesign::Pad×3, PartDesign::Pocket×1, PartDesign::Body×1, Spreadsheet::Sheet×1
note: 13 computed .brp shape members not serialized (recipe doc carries the construction recipe); baked Part::Feature solids carry a one-line shape summary decoded from their .brp

FEATURE [Sketcher::SketchObject] Sketch026
  FullyConstrained = true
  MapMode = 5
  Support = -> [XY_Plane051]
  sketch-geometry (12):
    g0: LineSegment StartX=39 StartY=33.5 StartZ=0 EndX=-39 EndY=33.5 EndZ=0
    g1: LineSegment StartX=-42 StartY=30.5 StartZ=0 EndX=-42 EndY=-30.5 EndZ=0
    g2: LineSegment StartX=-39 StartY=-33.5 StartZ=0 EndX=39 EndY=-33.5 EndZ=0
    g3: LineSegment StartX=42 StartY=-30.5 StartZ=0 EndX=42 EndY=30.5 EndZ=0
    g4: ArcOfCircle CenterX=39 CenterY=-30.5 CenterZ=0 NormalX=0 NormalY=0 NormalZ=1 AngleXU=0 Radius=3 StartAngle=4.71239 EndAngle=6.28319
    g5: GeomPoint X=42 Y=-33.5 Z=0
    g6: ArcOfCircle CenterX=39 CenterY=30.5 CenterZ=0 NormalX=0 NormalY=0 NormalZ=1 AngleXU=0 Radius=3 StartAngle=2.76e-14 EndAngle=1.5708
    g7: GeomPoint X=42 Y=33.5 Z=0
    g8: ArcOfCircle CenterX=-39 CenterY=30.5 CenterZ=0 NormalX=0 NormalY=0 NormalZ=1 AngleXU=0 Radius=3 StartAngle=1.5708 EndAngle=3.14159
    g9: GeomPoint X=-42 Y=33.5 Z=0
    g10: ArcOfCircle CenterX=-39 CenterY=-30.5 CenterZ=0 NormalX=0 NormalY=0 NormalZ=1 AngleXU=0 Radius=3 StartAngle=3.14159 EndAngle=4.71239
    g11: GeomPoint X=-42 Y=-33.5 Z=0
  constraints (27):
    c: Horizontal(g0)
    c: Horizontal(g2)
    c: Vertical(g1)
    c: Vertical(g3)
    c: Symmetric(g9,g5,g-1)
    c: PointOnObject(g5,g3)
    c: PointOnObject(g5,g2)
    c: Tangent(g3,g4) = -1.5708
    c: Tangent(g2,g4) = -1.5708
    c: PointOnObject(g7,g3)
    c: PointOnObject(g7,g0)
    c: Tangent(g3,g6) = -1.5708
    c: Tangent(g0,g6) = -1.5708
    c: PointOnObject(g9,g0)
    c: PointOnObject(g9,g1)
    c: Tangent(g0,g8) = -1.5708
    c: Tangent(g1,g8) = -1.5708
    c: PointOnObject(g11,g1)
    c: PointOnObject(g11,g2)
    c: Tangent(g1,g10) = -1.5708
    c: Tangent(g2,g10) = -1.5708
    c: DistanceY(g2,g0) = 67
    c: DistanceX(g1,g3) = 84
    c: Equal(g6,g4)
    c: Equal(g4,g10)
    c: Equal(g10,g8)
    c: Diameter(g4) = 6
FEATURE [PartDesign::Pad] Pad009  label="YukonMainBoard"
  Direction = (0,0,1)
  Length = 1.6
  Length2 = 10
  Profile = -> Sketch026
  ReferenceAxis = -> Sketch026 [N_Axis]
  Type = 0
FEATURE [Sketcher::SketchObject] Sketch027
  ExternalGeometry = -> [Pad009]
  FullyConstrained = true
  MapMode = 5
  Placement = pos=(0,0,1.6) rot=(0,0,1;0rad)
  Support = -> [Pad009]
  sketch-geometry (4):
    g0: Circle CenterX=-39 CenterY=30.5 CenterZ=0 NormalX=0 NormalY=0 NormalZ=1 AngleXU=0 Radius=1.25
    g1: Circle CenterX=39 CenterY=30.5 CenterZ=0 NormalX=0 NormalY=0 NormalZ=1 AngleXU=0 Radius=1.25
    g2: Circle CenterX=39 CenterY=-30.5 CenterZ=0 NormalX=0 NormalY=0 NormalZ=1 AngleXU=0 Radius=1.25
    g3: Circle CenterX=-39 CenterY=-30.5 CenterZ=0 NormalX=0 NormalY=0 NormalZ=1 AngleXU=0 Radius=1.25
  constraints (9):
    c: Symmetric(g3,g2,g-2)
    c: Symmetric(g2,g1,g-1)
    c: Symmetric(g3,g0,g-1)
    c: Equal(g0,g3)
    c: Equal(g3,g2)
    c: Equal(g2,g1)
    c: Diameter(g1) = 2.5
    c: DistanceX(g0,g1) = 78
    c: DistanceY(g2,g1) = 61
FEATURE [PartDesign::Pocket] Pocket010  label="YukonMountingHoles"
  BaseFeature = -> Pad009
  Direction = (0,0,-1)
  Length = 5
  Length2 = 5
  Profile = -> Sketch027
  ReferenceAxis = -> Sketch027 [N_Axis]
  Type = 1
FEATURE [Sketcher::SketchObject] Sketch028
  ExternalGeometry = -> [Pocket010]
  FullyConstrained = true
  MapMode = 5
  Placement = pos=(0,0,1.6) rot=(0,0,1;0rad)
  Support = -> [Pocket010]
  sketch-geometry (1):
    g0: Circle CenterX=12 CenterY=0 CenterZ=0 NormalX=0 NormalY=0 NormalZ=1 AngleXU=0 Radius=5
  constraints (3):
    c: PointOnObject(g0,g-1)
    c: Diameter(g0) = 10
    c: DistanceX(g0,g-3) = 30
FEATURE [PartDesign::Pad] Pad010  label="YukonCap"
  BaseFeature = -> Pocket010
  Direction = (0,0,1)
  Length = 10
  Length2 = 10
  Profile = -> Sketch028
  ReferenceAxis = -> Sketch028 [N_Axis]
  Type = 0
FEATURE [Sketcher::SketchObject] Sketch029
  ExternalGeometry = -> [Pad010]
  FullyConstrained = true
  MapMode = 5
  Placement = pos=(0,0,1.6) rot=(0,0,1;0rad)
  Support = -> [Pad010]
  sketch-geometry (8):
    g0: LineSegment StartX=-31.5 StartY=33.5 StartZ=0 EndX=31.5 EndY=33.5 EndZ=0
    g1: LineSegment StartX=31.5 StartY=33.5 StartZ=0 EndX=31.5 EndY=9.5 EndZ=0
    g2: LineSegment StartX=31.5 StartY=9.5 StartZ=0 EndX=-31.5 EndY=9.5 EndZ=0
    g3: LineSegment StartX=-31.5 StartY=9.5 StartZ=0 EndX=-31.5 EndY=33.5 EndZ=0
    g4: LineSegment StartX=31.5 StartY=-33.5 StartZ=0 EndX=-31.5 EndY=-33.5 EndZ=0
    g5: LineSegment StartX=-31.5 StartY=-33.5 StartZ=0 EndX=-31.5 EndY=-9.5 EndZ=0
    g6: LineSegment StartX=-31.5 StartY=-9.5 StartZ=0 EndX=31.5 EndY=-9.5 EndZ=0
    g7: LineSegment StartX=31.5 StartY=-9.5 StartZ=0 EndX=31.5 EndY=-33.5 EndZ=0
  constraints (22):
    c: Coincident(g0,g1)
    c: Coincident(g1,g2)
    c: Coincident(g2,g3)
    c: Coincident(g3,g0)
    c: Horizontal(g0)
    c: Horizontal(g2)
    c: Vertical(g1)
    c: Vertical(g3)
    c: PointOnObject(g0,g-3)
    c: Coincident(g4,g5)
    c: Coincident(g5,g6)
    c: Coincident(g6,g7)
    c: Coincident(g7,g4)
    c: Horizontal(g4)
    c: Vertical(g5)
    c: Vertical(g7)
    c: PointOnObject(g4,g-4)
    c: Symmetric(g6,g1,g-1)
    c: DistanceX(g6,g6) = 63
    c: Equal(g2,g6)
    c: DistanceY(g5,g5) = 24
    c: Symmetric(g5,g6,g-2)
FEATURE [PartDesign::Pad] Pad011  label="YukonModules"
  BaseFeature = -> Pad010
  Direction = (0,0,1)
  Length = 17
  Length2 = 10
  Profile = -> Sketch029
  ReferenceAxis = -> Sketch029 [N_Axis]
  Type = 0
FEATURE [PartDesign::Body] Body008  label="Yukon"
  Group = -> [Sketch026,Pad009,Sketch027,Pocket010,Sketch028,Pad010,Sketch029,Pad011]
  Origin = -> Origin051
  Tip = -> Pad011
FEATURE [Spreadsheet::Sheet] Spreadsheet  label="YukonSheet"
  cells = A1='Yukon Holes; D1='Board; A2='width_spacing; B2(width_spacing)==61 mm; D2='width; E2(width)==67 mm; A3='hole_diam; B3(hole_diam)==2.5 mm; D3='length; E3(length)==84 mm; A4='length_spacing; B4(length_spacing)==78 mm
COMPONENT P5 — recipe-attached ("YukonRLeftStandoff", modeled in this document).
Construction recipe (the document's own serialized feature program — sketch geometry with constraints, then the solid features built on it; lengths are millimeters unless a unit is written):

FEATURE [Sketcher::SketchObject] Sketch030  label="M25StandoffBodySketch"
  FullyConstrained = true
  MapMode = 5
  Support = -> [XY_Plane052]
  sketch-geometry (7):
    g0: LineSegment StartX=1.37121 StartY=-2.375 StartZ=0 EndX=2.74241 EndY=0 EndZ=0
    g1: LineSegment StartX=2.74241 StartY=0 StartZ=0 EndX=1.37121 EndY=2.375 EndZ=0
    g2: LineSegment StartX=1.37121 StartY=2.375 StartZ=0 EndX=-1.37121 EndY=2.375 EndZ=0
    g3: LineSegment StartX=-1.37121 StartY=2.375 StartZ=0 EndX=-2.74241 EndY=0 EndZ=0
    g4: LineSegment StartX=-2.74241 StartY=0 StartZ=0 EndX=-1.37121 EndY=-2.375 EndZ=0
    g5: LineSegment StartX=-1.37121 StartY=-2.375 StartZ=0 EndX=1.37121 EndY=-2.375 EndZ=0
    g6: Circle CenterX=0 CenterY=0 CenterZ=0 NormalX=0 NormalY=0 NormalZ=1 AngleXU=0 Radius=2.74241
  constraints (16):
    c: Coincident(g0,g1)
    c: Coincident(g1,g2)
    c: Coincident(g2,g3)
    c: Coincident(g3,g4)
    c: Coincident(g4,g5)
    c: Coincident(g5,g0)
    c: Equal(g0, g1-g5) x5
    c: PointOnObject(g0,g6)
    c: PointOnObject(g1,g6)
    c: PointOnObject(g2,g6)
    c: PointOnObject(g3,g6)
    c: PointOnObject(g4,g6)
    c: PointOnObject(g5,g6)
    c: Coincident(g6,g-1)
    c: PointOnObject(g0,g-1)
    c: DistanceY(g4,g2) = 4.75
FEATURE [PartDesign::Pad] Pad012  label="M25StandoffBody"
  Direction = (0,0,1)
  Length = 18
  Length2 = 10
  Profile = -> Sketch030
  ReferenceAxis = -> Sketch030 [N_Axis]
  Type = 0
FEATURE [Sketcher::SketchObject] Sketch031  label="M25StandoffThreadSketch"
  FullyConstrained = true
  MapMode = 5
  Placement = pos=(0,0,0) rot=(1,0,0;3.14159rad)
  Support = -> [Pad012]
  sketch-geometry (1):
    g0: Circle CenterX=0 CenterY=0 CenterZ=0 NormalX=0 NormalY=0 NormalZ=1 AngleXU=0 Radius=1.25
  constraints (2):
    c: Coincident(g0,g-1)
    c: Diameter(g0) = 2.5
FEATURE [PartDesign::Pad] Pad013  label="M25StandoffThread"
  BaseFeature = -> Pad012
  Direction = (0,0,-1)
  Length = 6
  Length2 = 10
  Profile = -> Sketch031
  ReferenceAxis = -> Sketch031 [N_Axis]
  Type = 0
FEATURE [PartDesign::Body] Body009  label="M25StandOff"
  Group = -> [Sketch030,Pad012,Sketch031,Pad013]
  Origin = -> Origin052
  Tip = -> Pad013
COMPONENT P6 — same part as P5; its construction recipe is shown at P5.
COMPONENT P7 — same part as P5; its construction recipe is shown at P5.
COMPONENT P8 — same part as P5; its construction recipe is shown at P5.
COMPONENT P9 — geometry summary ("MountingPlatePart"; no construction recipe available for this part):
  bounding box: 110.0 x 84.0 x 8.0 mm
  tessellated surface: 716 triangles
  volume: 47200 mm^3 (64% of its bounding box)
COMPONENT P10 — geometry summary ("Gearbox"; no construction recipe available for this part):
  bounding box: 44.5 x 37.3 x 22.4 mm
  tessellated surface: 1,136 triangles
  volume: 8432 mm^3 (23% of its bounding box)
COMPONENT P11 — geometry summary ("USBBatteryAssembly"; no construction recipe available for this part):
  bounding box: 104.0 x 99.0 x 23.0 mm
  tessellated surface: 1,812 triangles
  volume: 190936 mm^3 (81% of its bounding box)
  symmetry: mirror-symmetric across its x mid-plane
COMPONENT P12 — geometry summary ("CameraAssembly2"; no construction recipe available for this part):
  bounding box: 65.0 x 46.8 x 40.0 mm
  tessellated surface: 2,818 triangles
  volume: 110954 mm^3 (91% of its bounding box)
COMPONENT P13 — geometry summary ("CameraMountPlate"; no construction recipe available for this part):
  bounding box: 90.0 x 46.8 x 13.0 mm
  tessellated surface: 660 triangles
  volume: 11753 mm^3 (21% of its bounding box)
  symmetry: mirror-symmetric across its x mid-plane
COMPONENT P14 — geometry summary ("PiNoonMountAssembly"; no construction recipe available for this part):
  bounding box: 65.0 x 29.5 x 26.0 mm
  tessellated surface: 524 triangles
  volume: 13513 mm^3 (27% of its bounding box)
  symmetry: mirror-symmetric across its x mid-plane
COMPONENT P15 — geometry summary ("sprocket_collar v1"; no construction recipe available for this part):
  bounding box: 35.0 x 7.3 x 7.0 mm
  tessellated surface: 32 triangles
  volume: 2025 mm^3 (113% of its bounding box)
  symmetry: 4-fold rotationally symmetric about the x axis; 2-fold rotationally symmetric about the y axis; 2-fold rotationally symmetric about the z axis; mirror-symmetric across its x mid-plane, y mid-plane, z mid-plane
PROVENANCE & LICENSES
A FreeCAD (.FCStd) document from a public repository crawl; recipes are the document's own serialized feature recipes (and, for linked parts, companion documents' recipes).
License: mit.
